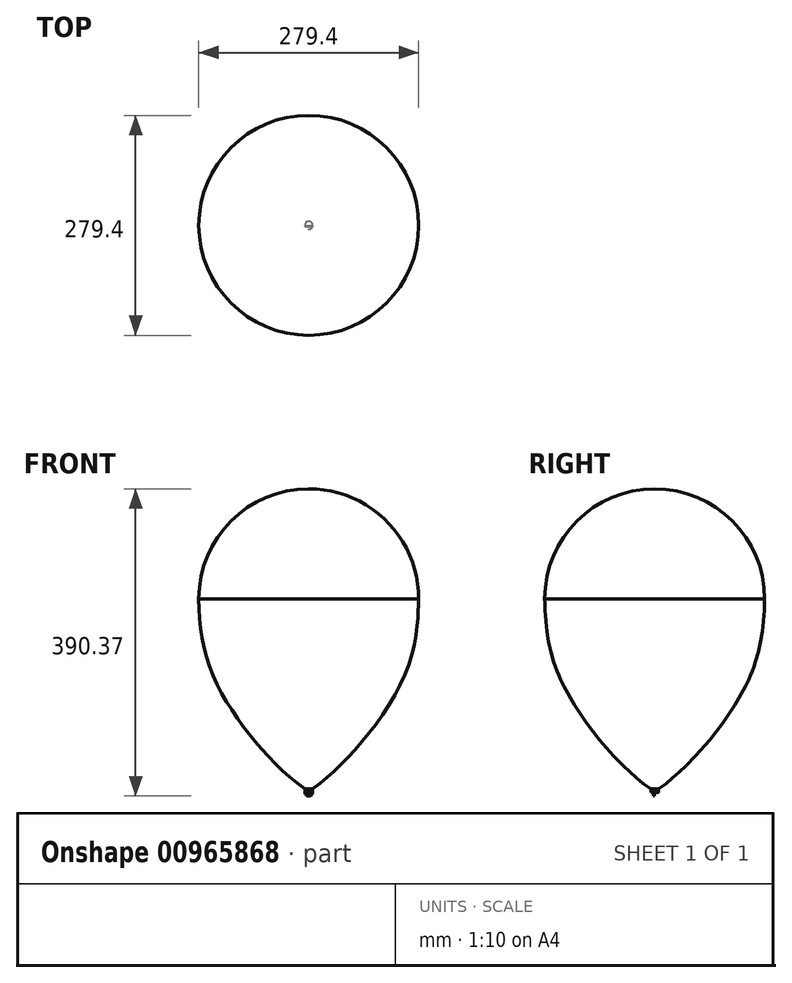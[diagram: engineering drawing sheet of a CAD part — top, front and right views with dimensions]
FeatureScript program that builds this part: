
annotation { "Feature Type Name" : "Feature", "Feature Type Description" : "" }
export const myFeature = defineFeature(function(context is Context, id is Id, definition is map)
    precondition{}
    {
        {
            var Q0;
            Q0=qCreatedBy(makeId("Front.planeOp"),FACE);
            var sketch = newSketch(context, id + "F0", { "sketchPlane" : qUnion([Q0])});
            skArc(sketch, "E0", {"start": v(0, 139.7) * mm, "mid": v(-98.78, 98.78) * mm, "end": v(-139.7, 0) * mm});
            skArc(sketch, "E1", {"start": v(0, 139.45) * mm, "mid": v(-98.6, 98.6) * mm, "end": v(-139.45, 0) * mm});
            skLineSegment(sketch, "E2", {"start": v(139.45, 0) * mm, "end": v(139.7, 0) * mm});
            skLineSegment(sketch, "E3", {"start": v(-139.45, 0) * mm, "end": v(-139.7, 0) * mm});
            skFitSpline(sketch, "E4", {"points": [v(-139.45, 0) * mm, v(-126.98, -82.3) * mm, v(-88.5, -154.3) * mm, v(-41.94, -209.23) * mm, v(0, -245) * mm], "startDerivative": vector(12.95, -304.22) * mm, "endDerivative": vector(163.17, -102.13) * mm});
            skLineSegment(sketch, "E5", {"start": v(0, 139.45) * mm, "end": v(0, 139.7) * mm});
            skPoint(sketch, "E5.endSnap0", {"position": v(0, 139.45) * mm});
            skFitSpline(sketch, "E6", {"points": [v(-139.7, 0) * mm, v(-138.3, -27.16) * mm, v(-127.5, -82.3) * mm, v(-88.93, -154.3) * mm, v(-42.45, -209.23) * mm, v(0, -245.36) * mm], "startDerivative": vector(6.11, -190.08) * mm, "endDerivative": vector(228.99, -159.32) * mm});
            skLineSegment(sketch, "E7", {"start": v(0, -245) * mm, "end": v(0, -245.36) * mm});
            skLineSegment(sketch, "E8", {"start": v(0, 139.7) * mm, "end": v(0, -245) * mm});
            skSolve(sketch);
        }
        {
            var Q0;
            {var subQ0=sQuery(id+"F0.wireOp",EDGE,"E0");Q0=makeQuery(id+"F0.imprint","IMPRINT",FACE,{"disambiguationData":[TD([[makeQuery(id+"F0.imprint","IMPRINT",EDGE,{"derivedFrom":subQ0}),1.0]])]});}
            var Q1;
            {var subQ0=sQuery(id+"F0.wireOp",EDGE,"E3");Q1=makeQuery(id+"F0.imprint","IMPRINT",FACE,{"disambiguationData":[TD([[makeQuery(id+"F0.imprint","IMPRINT",EDGE,{"derivedFrom":subQ0}),1.0]])]});}
            var Q2;
            {var subQ0=sQuery(id+"F0.wireOp",EDGE,"E6");var subQ1=sQuery(id+"F0.wireOp",EDGE,"E4");var subQ2=makeQuery(id+"F0.imprint","INTERSECT",VERTEX,{"disambiguationData":[OD(0.0)],"derivedFrom":[subQ1,subQ0]});Q2=makeQuery(id+"F0.imprint","IMPRINT",FACE,{"disambiguationData":[TD([[makeQuery(id+"F0.imprint","IMPRINT",EDGE,{"disambiguationData":[TD([[subQ2,-1.0]])],"derivedFrom":subQ1}),1.0]])]});}
            var Q3;
            {var subQ0=sQuery(id+"F0.wireOp",EDGE,"E7");Q3=makeQuery(id+"F0.imprint","IMPRINT",FACE,{"disambiguationData":[TD([[makeQuery(id+"F0.imprint","IMPRINT",EDGE,{"derivedFrom":subQ0}),-1.0]])]});}
            var Q4;
            Q4=sQuery(id+"F0.wireOp",EDGE,"E8");
            revolve(context, id + "F1", {"surfaceOperationType" : NewSurfaceOperationType.NEW, "entities" : qUnion([Q0, Q1, Q2, Q3]), "axis" : qUnion([Q4]), "revolveType" : RevolveType.FULL});
        }
        {
            var Q0;
            Q0=qCreatedBy(makeId("Top.planeOp"),FACE);
            cPlane(context, id + "F2", {"entities" : qUnion([Q0]), "cplaneType" : CPlaneType.OFFSET, "offset" : 241.3 * mm, "oppositeDirection" : true, "width" : 152.4 * mm, "height" : 152.4 * mm});
        }
        {
            var Q0;
            Q0=qCreatedBy(id+"F2.planeOp",FACE);
            var sketch = newSketch(context, id + "F3", { "sketchPlane" : qUnion([Q0])});
            skCircle(sketch, "E9", {"center": v(0, 0) * mm, "radius": 5.03 * mm});
            skSolve(sketch);
        }
        {
            var Q0;
            Q0=qSketchRegion(id+"F3",true);
            extrude(context, id + "F4", {"entities" : qUnion([Q0]), "operationType" : NewBodyOperationType.ADD, "depth" : 25.4 * mm, "offsetDistance" : 25.4 * mm});
        }
        {
            var Q0;
            Q0=qSketchRegion(id+"F3",true);
            extrude(context, id + "F5", {"entities" : qUnion([Q0]), "operationType" : NewBodyOperationType.ADD, "oppositeDirection" : true, "depth" : 4.32 * mm, "offsetDistance" : 25.4 * mm});
        }
        {
            var Q0;
            Q0=qCreatedBy(makeId("Front.planeOp"),FACE);
            var sketch = newSketch(context, id + "F6", { "sketchPlane" : qUnion([Q0])});
            skArc(sketch, "E10", {"start": v(-3.25, -245.63) * mm, "mid": v(0.02, -248.89) * mm, "end": v(3.25, -245.6) * mm});
            skArc(sketch, "E11", {"start": v(-5.03, -245.64) * mm, "mid": v(0.03, -250.67) * mm, "end": v(5.03, -245.59) * mm});
            skLineSegment(sketch, "E12", {"start": v(5.03, -245.59) * mm, "end": v(-5.03, -245.64) * mm});
            skSolve(sketch);
        }
        {
            var Q0;
            {var subQ0=sQuery(id+"F6.wireOp",EDGE,"E10");Q0=makeQuery(id+"F6.imprint","IMPRINT",FACE,{"disambiguationData":[TD([[makeQuery(id+"F6.imprint","IMPRINT",EDGE,{"derivedFrom":subQ0}),-1.0]])]});}
            extrude(context, id + "F7", {"entities" : qUnion([Q0]), "operationType" : NewBodyOperationType.ADD, "depth" : 1.27 * mm, "offsetDistance" : 25.4 * mm});
        }
    });
